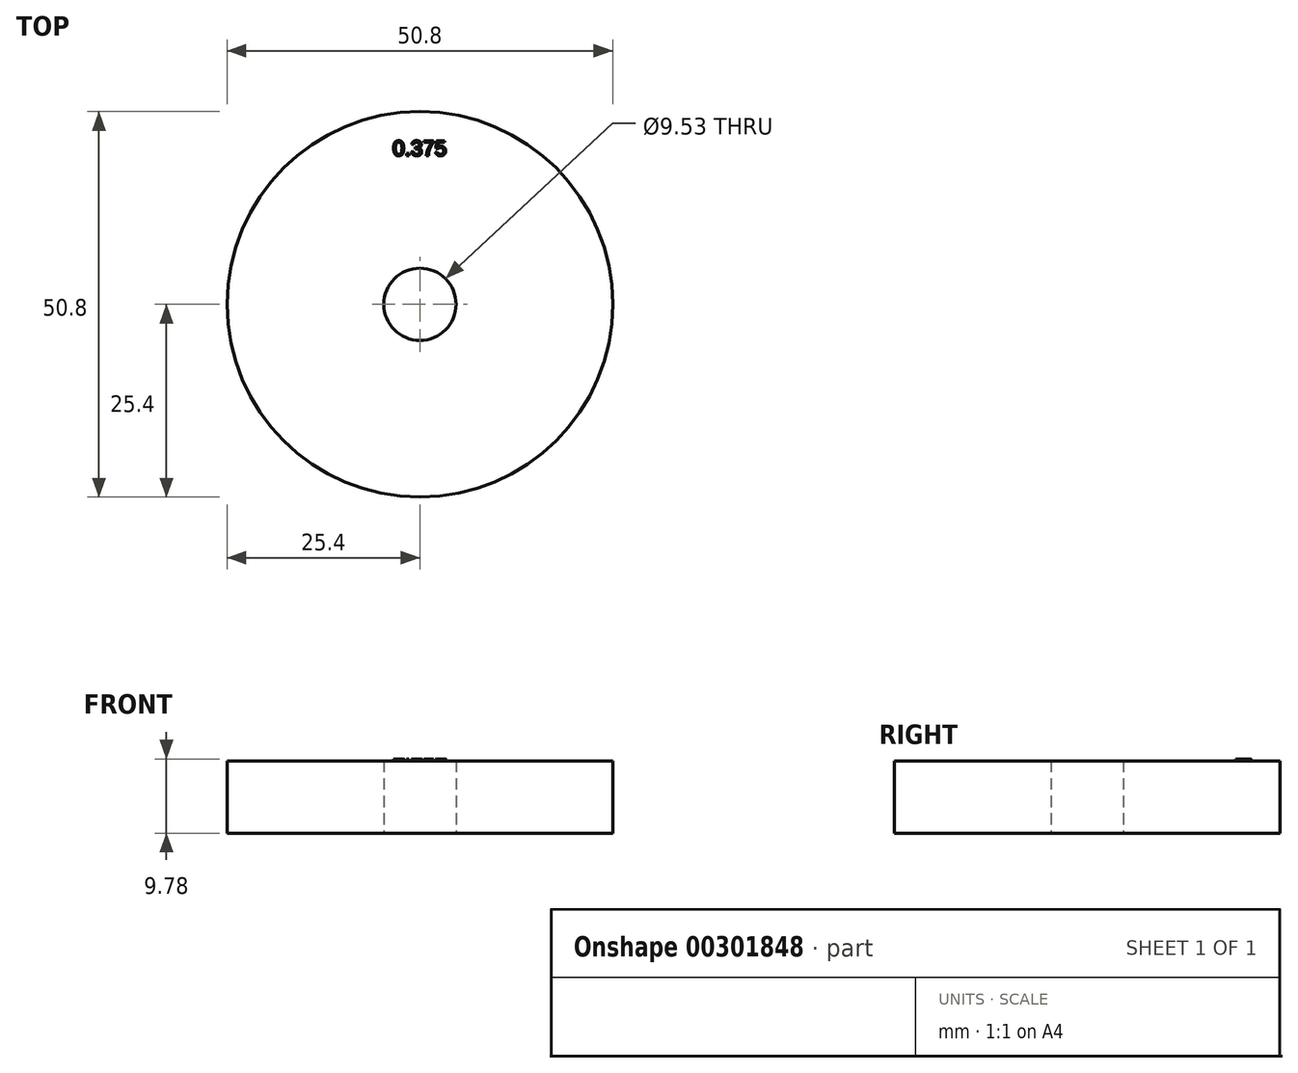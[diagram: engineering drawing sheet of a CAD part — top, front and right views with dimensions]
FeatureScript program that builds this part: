
annotation { "Feature Type Name" : "Feature", "Feature Type Description" : "" }
export const myFeature = defineFeature(function(context is Context, id is Id, definition is map)
    precondition{}
    {
        {
            var Q0;
            Q0=qCreatedBy(makeId("Top.planeOp"),FACE);
            var sketch = newSketch(context, id + "F0", { "sketchPlane" : qUnion([Q0])});
            skCircle(sketch, "E0", {"center": v(0, 0) * mm, "radius": 25.4 * mm});
            skCircle(sketch, "E1", {"center": v(0, 0) * mm, "radius": 4.76 * mm});
            skSolve(sketch);
        }
        {
            var Q0;
            Q0=qSketchRegion(id+"F0",true);
            extrude(context, id + "F1", {"entities" : qUnion([Q0]), "depth" : 9.52 * mm});
        }
        {
            var Q0;
            Q0=makeQuery(id+"F1.opExtrude","CAP_FACE",FACE,{"disambiguationData":[OSD([sQuery(id+"F0.wireOp",EDGE,"E0"),sQuery(id+"F0.wireOp",EDGE,"E1")])],"isStart":false});
            var sketch = newSketch(context, id + "F2", { "sketchPlane" : qUnion([Q0])});
            skText(sketch, "E2", { "text": "0.375", "fontName": "Arimo-Regular.ttf"});
            const initialGuessF2  = {"E2": [-0.00358, 0.0196, 1, 0, 0.00204]};
            skSetInitialGuess(sketch, initialGuessF2);
            skSolve(sketch);
        }
        {
            var Q0;
            Q0 = qSketchRegion(id + "F2", true);
            extrude(context, id + "F3", {"entities" : qUnion([Q0]), "operationType" : NewBodyOperationType.ADD, "depth" : 0.25 * mm});
        }
    });
